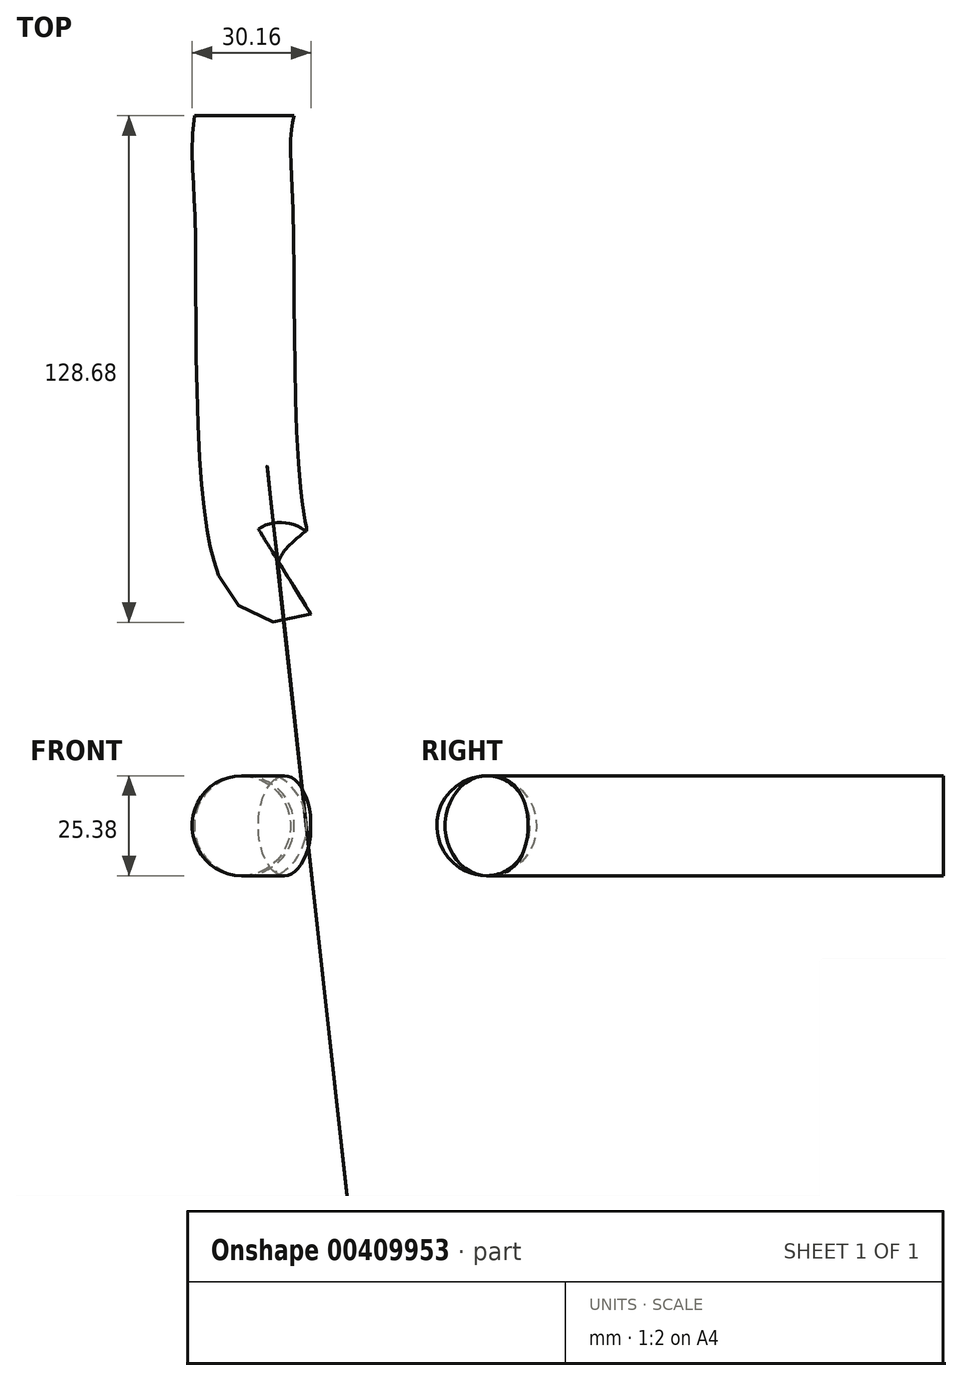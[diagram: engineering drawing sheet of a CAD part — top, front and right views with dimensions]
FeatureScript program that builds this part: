
annotation { "Feature Type Name" : "Feature", "Feature Type Description" : "" }
export const myFeature = defineFeature(function(context is Context, id is Id, definition is map)
    precondition{}
    {
        {
            var Q0;
            Q0=qCreatedBy(makeId("Front.planeOp"),FACE);
            var sketch = newSketch(context, id + "F0", { "sketchPlane" : qUnion([Q0])});
            skCircle(sketch, "E0", {"center": v(0, 0) * mm, "radius": 12.69 * mm});
            skSolve(sketch);
        }
        {
            var Q0;
            Q0=qCreatedBy(makeId("Top.planeOp"),FACE);
            var sketch = newSketch(context, id + "F1", { "sketchPlane" : qUnion([Q0])});
            skFitSpline(sketch, "E1", {"points": [v(0, 0) * mm, v(0, -28.14) * mm, v(10.24, -115.79) * mm], "startDerivative": vector(-11.84, -68.37) * mm, "endDerivative": vector(54.04, 21.68) * mm});
            skSolve(sketch);
        }
        {
            var Q0;
            Q0=qCreatedBy(makeId("Front.planeOp"),FACE);
            cPlane(context, id + "F2", {"entities" : qUnion([Q0]), "cplaneType" : CPlaneType.OFFSET, "offset" : 101.6 * mm, "width" : 152.4 * mm, "height" : 152.4 * mm});
        }
        {
            var Q0;
            Q0=makeQuery(id+"F0.imprint","IMPRINT",FACE,{"disambiguationData":[TD([[makeQuery(id+"F0.imprint","IMPRINT",EDGE,{"derivedFrom":sQuery(id+"F0.wireOp",EDGE,"E0")}),1.0]])]});
            var Q1;
            Q1=sQuery(id+"F0.wireOp",EDGE,"E0");
            var Q2;
            Q2=sQuery(id+"F1.wireOp",EDGE,"E1");
            sweep(context, id + "F3", {"profiles" : qUnion([Q0]), "surfaceProfiles" : qUnion([Q1]), "path" : qUnion([Q2])});
        }
    });
